# Revit family: XLN 600 7000 840 ALO (OP)
name_source: partatom
category: Oprawy oświetleniowe
units: mm (PartAtom-declared; Revit-internal decimal feet)

## family parameters
Numer OmniClass = 23.80.70.00
Oparty na płaszczyźnie roboczej = Nie
Punkt obliczania pomieszczeń = Nie
Tnij formami wycięć po wczytaniu = Nie
Typ części = Normalny
Tytuł OmniClass = Lighting
Współdzielony = Nie
Wymiar okrągłego złącza = Użyj średnicy
Zawsze pionowo = Tak
Źródło światła = Tak

## types (1)
- XLN 600 7000 840 ALO (OP)
    Domyślna rzędna = 0 mm  [stored 0 ft]
    Emituj kształt widoczny w renderingu = Nie
    Emituj z długości prostokąta = 595 mm  [stored 1.9521 ft]
    Emituj z szerokości prostokąta = 595 mm  [stored 1.9521 ft]
    Filtr koloru = 16777215
    Odchylenie kierunku = 90.00°
    Plik sieci fotometrycznej = XLN 600 7000 840 ALO (OP)_LDT.ies
    Zmiana temperatury barwowej przyciemniania lampy = <Brak>

note: [stored X ft] marks values corroborated as IEEE doubles in the binary element streams (Revit-internal decimal feet)
